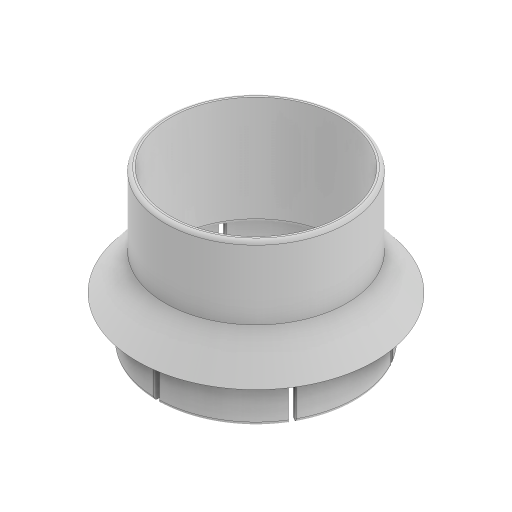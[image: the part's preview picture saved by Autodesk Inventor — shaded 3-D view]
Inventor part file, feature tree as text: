
AUTODESK INVENTOR PART (.ipt)
format: ipt  version: 2023 (Build 270158000, 158)  size: 216,064 bytes
history: native  units: mm
features: sketch x2, revolve x1, extrude x1, pattern_circular x1
ambient origin geometry x8: Origin, YZ Plane, XZ Plane, XY Plane, X Axis, Y Axis, Z Axis, Center Point
bodies: Solid1 (feature_tree)
feature tree (5):
  revolve  "Revolution1"  [1 undecoded]
  extrude  "Extrusion1"  Depth=3.0mm
  pattern_circular  "Circular Pattern1"  [2 undecoded]
  sketch  "Sketch1"  dims[d7=40.0mm d10=2.0mm]
  sketch  "Sketch2"  dims[d11=90.0deg d12=20.0mm d13=3.0mm d14=10.0mm d15=25.0mm d16=0.0mm d17=60.0mm d18=360.0deg d20=50.0mm d21=54.7mm d22=3.0mm d23=2.0mm d24=4.0mm]
note: 3 required parameter values undecoded (feature->parameter linkage not recoverable at this tier; creation-order binding heuristic only, values carry confidence <= 0.55)